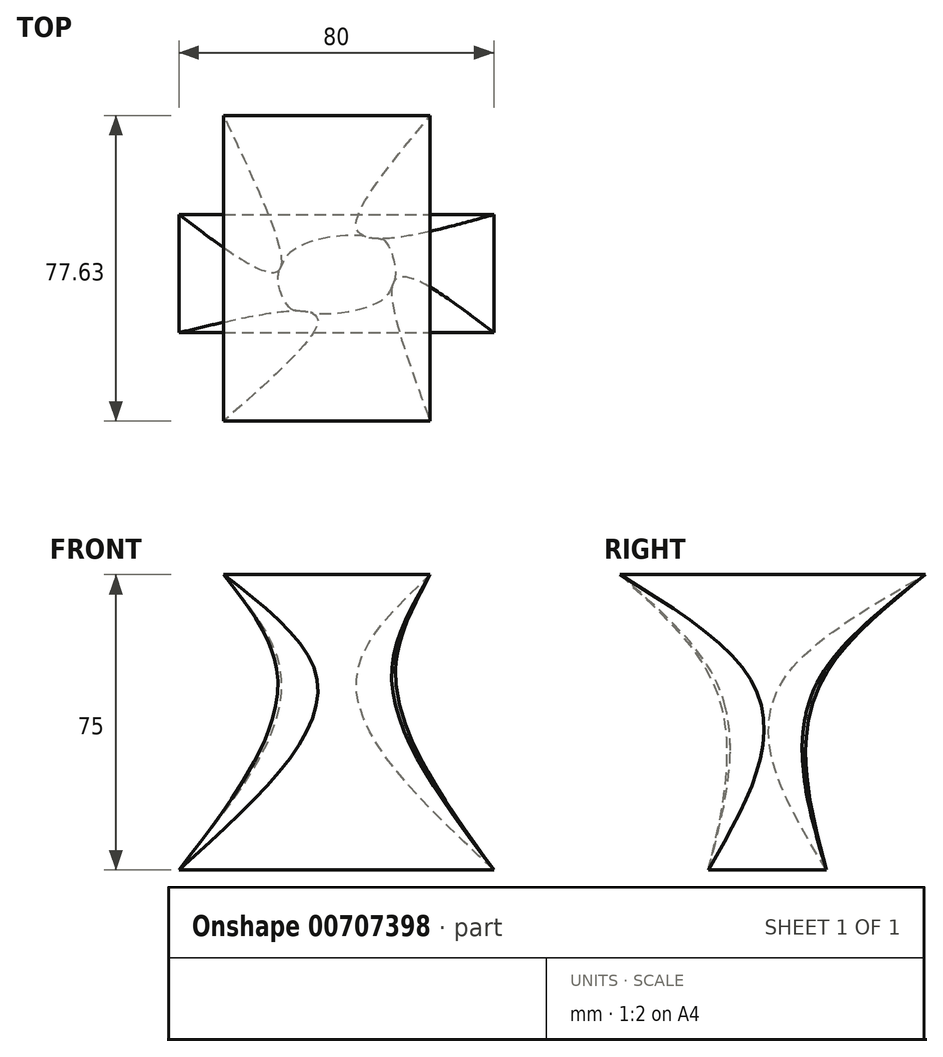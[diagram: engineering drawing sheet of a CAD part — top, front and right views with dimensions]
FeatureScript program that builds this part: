
annotation { "Feature Type Name" : "Feature", "Feature Type Description" : "" }
export const myFeature = defineFeature(function(context is Context, id is Id, definition is map)
    precondition{}
    {
        {
            var Q0;
            Q0=qCreatedBy(makeId("Top.planeOp"),FACE);
            var sketch = newSketch(context, id + "F0", { "sketchPlane" : qUnion([Q0])});
            skLineSegment(sketch, "E0.bottom", {"start": v(-40, 15) * mm, "end": v(40, 15) * mm});
            skLineSegment(sketch, "E0.top", {"start": v(-40, -15) * mm, "end": v(40, -15) * mm});
            skLineSegment(sketch, "E0.left", {"start": v(-40, 15) * mm, "end": v(-40, -15) * mm});
            skLineSegment(sketch, "E0.right", {"start": v(40, 15) * mm, "end": v(40, -15) * mm});
            skSolve(sketch);
        }
        {
            var Q0;
            Q0=qCreatedBy(makeId("Top.planeOp"),FACE);
            cPlane(context, id + "F1", {"entities" : qUnion([Q0]), "cplaneType" : CPlaneType.OFFSET, "offset" : 50 * mm, "width" : 150 * mm, "height" : 150 * mm});
        }
        {
            var Q0;
            Q0=qCreatedBy(id+"F1.planeOp",FACE);
            var sketch = newSketch(context, id + "F2", { "sketchPlane" : qUnion([Q0])});
            skCircle(sketch, "E1", {"center": v(0, 0) * mm, "radius": 15 * mm});
            skSolve(sketch);
        }
        {
            var Q0;
            Q0=qCreatedBy(id+"F1.planeOp",FACE);
            cPlane(context, id + "F3", {"entities" : qUnion([Q0]), "cplaneType" : CPlaneType.OFFSET, "offset" : 25 * mm, "width" : 150 * mm, "height" : 150 * mm});
        }
        {
            var Q0;
            Q0=qCreatedBy(id+"F3.planeOp",FACE);
            var sketch = newSketch(context, id + "F4", { "sketchPlane" : qUnion([Q0])});
            skLineSegment(sketch, "E2.bottom", {"start": v(-28.6, -37.48) * mm, "end": v(23.85, -37.48) * mm});
            skLineSegment(sketch, "E2.top", {"start": v(-28.6, 40.15) * mm, "end": v(23.85, 40.15) * mm});
            skLineSegment(sketch, "E2.left", {"start": v(-28.6, -37.48) * mm, "end": v(-28.6, 40.15) * mm});
            skLineSegment(sketch, "E2.right", {"start": v(23.85, -37.48) * mm, "end": v(23.85, 40.15) * mm});
            skSolve(sketch);
        }
        {
            var Q0;
            Q0=makeQuery(id+"F0.imprint","IMPRINT",FACE,{"disambiguationData":[TD([[makeQuery(id+"F0.imprint","IMPRINT",EDGE,{"derivedFrom":sQuery(id+"F0.wireOp",EDGE,"E0.bottom")}),-1.0]])]});
            var Q1;
            Q1=makeQuery(id+"F2.imprint","IMPRINT",FACE,{"disambiguationData":[TD([[makeQuery(id+"F2.imprint","IMPRINT",EDGE,{"derivedFrom":sQuery(id+"F2.wireOp",EDGE,"E1")}),1.0]])]});
            var Q2;
            Q2=makeQuery(id+"F4.imprint","IMPRINT",FACE,{"disambiguationData":[TD([[makeQuery(id+"F4.imprint","IMPRINT",EDGE,{"derivedFrom":sQuery(id+"F4.wireOp",EDGE,"E2.bottom")}),1.0]])]});
            loft(context, id + "F5", {"sheetProfilesArray" : [{ "sheetProfileEntities" : qUnion([Q0]) }, { "sheetProfileEntities" : qUnion([Q1]) }, { "sheetProfileEntities" : qUnion([Q2]) }]});
        }
    });
